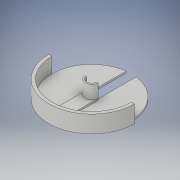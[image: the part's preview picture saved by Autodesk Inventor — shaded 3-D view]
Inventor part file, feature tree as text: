
AUTODESK INVENTOR PART (.ipt)
format: ipt  version: 2017 (Build 210142000, 142)  size: 159,744 bytes
history: native  units: in
note: dims shown in document units (in); Inventor stores cm internally (conversion verified against a paired STEP export)
features: extrude x7, sketch x7
ambient origin geometry x8: Origin, YZ Plane, XZ Plane, XY Plane, X Axis, Y Axis, Z Axis, Center Point
bodies: Solid1 (feature_tree)
feature tree (14):
  extrude  "Extrusion1"  Depth=1.1024in TaperAngle=0.0deg
  extrude  "Extrusion2"  Depth=1.1024in TaperAngle=0.0deg
  extrude  "Extrusion3"  Depth=0.9843in TaperAngle=0.0deg
  extrude  "Extrusion4"  Depth=0.6496in
  extrude  "Extrusion5"  Depth=1.1811in TaperAngle=0.0deg
  extrude  "Extrusion6"  [1 undecoded]
  extrude  "Extrusion7"  [1 undecoded]
  sketch  "Sketch1"  dims[d0=5.5118in d1=1.1024in d2=0.0in]
  sketch  "Sketch2"  dims[d3=0.6496in d4=1.1024in d5=0.0in]
  sketch  "Sketch3"  dims[d6=5.1181in d7=0.8268in d8=0.9843in d9=0.0in d10=8.6614in d11=0.0in]
  sketch  "Sketch4"  dims[d12=0.1181in d13=0.0in d14=0.6496in]
  sketch  "Sketch5"  dims[d15=1.1811in d16=0.0in d17=1.1811in d18=0.0in]
  sketch  "Sketch6"
  sketch  "Sketch8"
note: 2 required parameter values undecoded (feature->parameter linkage not recoverable at this tier; creation-order binding heuristic only, values carry confidence <= 0.55)
